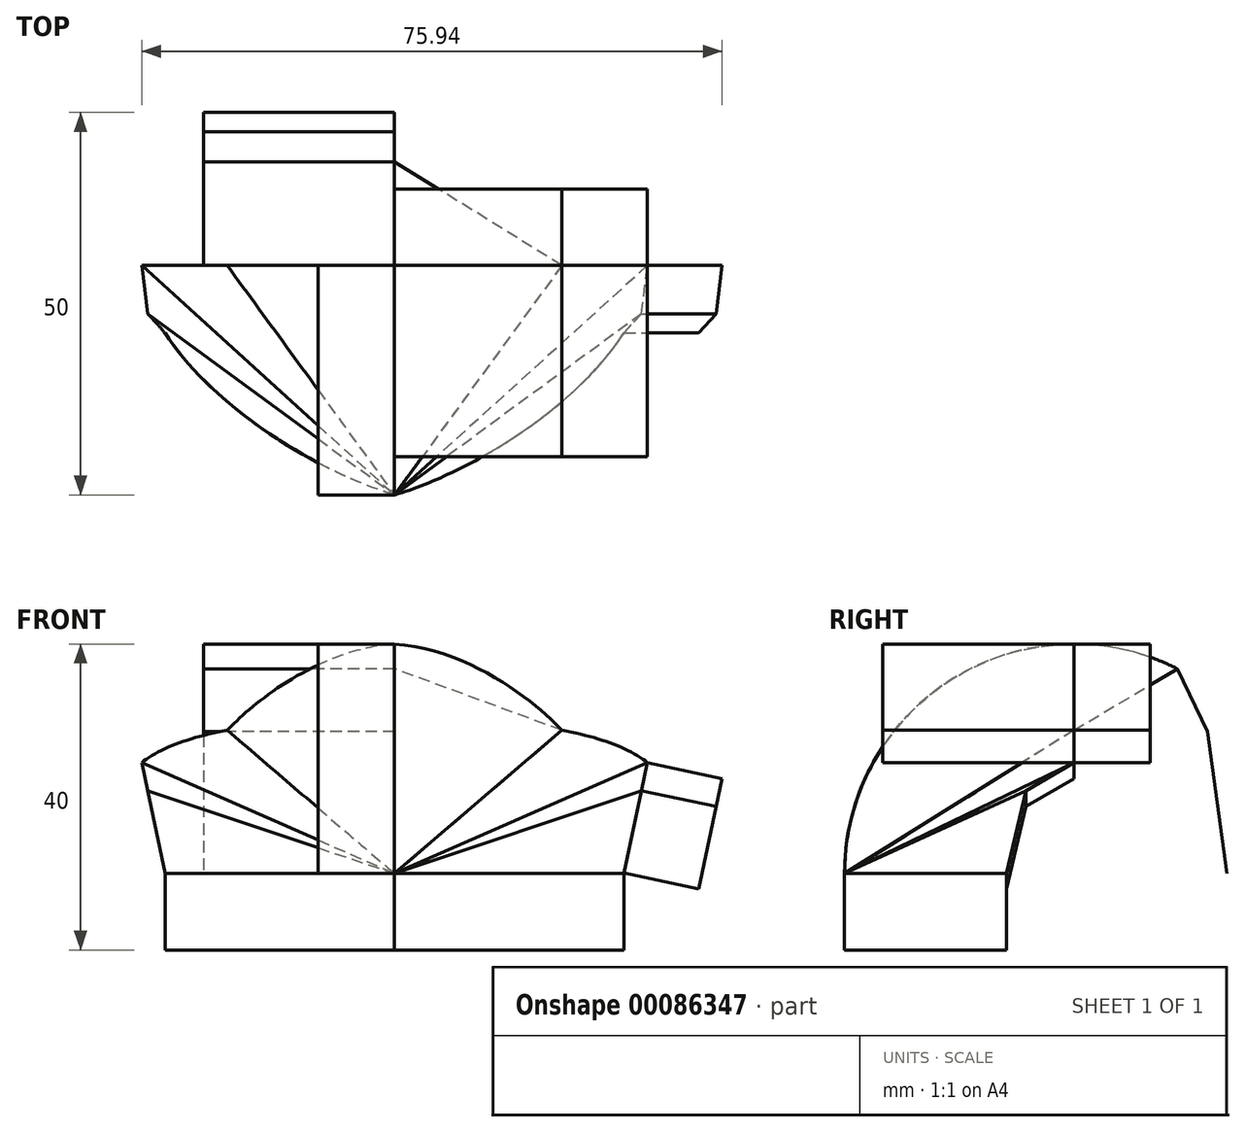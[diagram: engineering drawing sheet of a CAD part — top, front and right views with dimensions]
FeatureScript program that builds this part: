
annotation { "Feature Type Name" : "Feature", "Feature Type Description" : "" }
export const myFeature = defineFeature(function(context is Context, id is Id, definition is map)
    precondition{}
    {
        {
            var Q0;
            Q0=qCreatedBy(makeId("Front.planeOp"),FACE);
            var sketch = newSketch(context, id + "F0", { "sketchPlane" : qUnion([Q0])});
            skLineSegment(sketch, "E0", {"start": v(0, 0) * mm, "end": v(0, 30) * mm});
            skLineSegment(sketch, "E1", {"start": v(0, 0) * mm, "end": v(30, 0) * mm});
            skLineSegment(sketch, "E2", {"start": v(30, 0) * mm, "end": v(33.08, 14.5) * mm});
            skFitSpline(sketch, "E3", {"points": [v(0, 30) * mm, v(21.88, 18.74) * mm], "startDerivative": vector(30.88, -2.18) * mm, "endDerivative": vector(9.24, -9.83) * mm});
            skFitSpline(sketch, "E4", {"points": [v(33.08, 14.5) * mm, v(21.88, 18.74) * mm], "startDerivative": vector(-6.7, 5.6) * mm, "endDerivative": vector(-14.4, 2.61) * mm});
            skSolve(sketch);
        }
        {
            var Q0;
            Q0=qCreatedBy(makeId("Right.planeOp"),FACE);
            var sketch = newSketch(context, id + "F1", { "sketchPlane" : qUnion([Q0])});
            skLineSegment(sketch, "E5", {"start": v(-30, 0) * mm, "end": v(0, 0) * mm});
            skArc(sketch, "E6", {"start": v(0, 30) * mm, "mid": v(-21.21, 21.21) * mm, "end": v(-30, 0) * mm});
            skLineSegment(sketch, "E7", {"start": v(0, 30) * mm, "end": v(0, 0) * mm});
            skSolve(sketch);
        }
        {
            var Q0;
            Q0=qCreatedBy(makeId("Right.planeOp"),FACE);
            var Q1;
            Q1=sQuery(id+"F0.wireOp",EDGE,"E2");
            cPlane(context, id + "F2", {"entities" : qUnion([Q0, Q1]), "cplaneType" : CPlaneType.LINE_ANGLE, "offset" : 150 * mm, "angle" : 0 * degree, "width" : 150 * mm, "height" : 150 * mm});
        }
        {
            var Q0;
            Q0=qCreatedBy(id+"F2.planeOp",FACE);
            var sketch = newSketch(context, id + "F3", { "sketchPlane" : qUnion([Q0])});
            skLineSegment(sketch, "E8", {"start": v(6.3, 17.32) * mm, "end": v(0, 21.05) * mm});
            skLineSegment(sketch, "E9", {"start": v(0, 21.05) * mm, "end": v(0, 6.32) * mm});
            skLineSegment(sketch, "E10", {"start": v(6.3, 17.32) * mm, "end": v(8.79, 6.32) * mm});
            skLineSegment(sketch, "E11", {"start": v(0, 6.32) * mm, "end": v(8.79, 6.32) * mm});
            skSolve(sketch);
        }
        {
            var Q0;
            Q0=qCreatedBy(makeId("Top.planeOp"),FACE);
            var sketch = newSketch(context, id + "F4", { "sketchPlane" : qUnion([Q0])});
            skFitSpline(sketch, "E12", {"points": [v(0, -30) * mm, v(30, -8.8) * mm], "startDerivative": vector(34.32, 10.34) * mm, "endDerivative": vector(16.09, 25.94) * mm});
            skSolve(sketch);
        }
        {
            var Q0;
            Q0=sQuery(id+"F0.wireOp",EDGE,"E4");
            var Q1;
            Q1=sQuery(id+"F0.wireOp",EDGE,"E3");
            extrude(context, id + "F5", {"bodyType" : ToolBodyType.SURFACE, "surfaceEntities" : qUnion([Q0, Q1]), "oppositeDirection" : true, "depth" : 10 * mm});
        }
        {
            var Q0;
            Q0=sQuery(id+"F4.wireOp",EDGE,"E12");
            extrude(context, id + "F6", {"bodyType" : ToolBodyType.SURFACE, "surfaceEntities" : qUnion([Q0]), "oppositeDirection" : true, "depth" : 10 * mm});
        }
        {
            var Q0;
            Q0=sQuery(id+"F1.wireOp",EDGE,"E6");
            extrude(context, id + "F7", {"bodyType" : ToolBodyType.SURFACE, "surfaceEntities" : qUnion([Q0]), "oppositeDirection" : true, "depth" : 10 * mm});
        }
        {
            var Q0;
            Q0=sQuery(id+"F3.wireOp",EDGE,"E8");
            var Q1;
            Q1=sQuery(id+"F3.wireOp",EDGE,"E10");
            extrude(context, id + "F8", {"bodyType" : ToolBodyType.SURFACE, "surfaceEntities" : qUnion([Q0, Q1]), "oppositeDirection" : true, "depth" : 10 * mm});
        }
        {
            var Q0;
            Q0=makeQuery(id+"F5.opExtrude","SWEPT_BODY",BODY,{"disambiguationData":[OSD([sQuery(id+"F0.wireOp",EDGE,"E3")])]});
            var Q1;
            Q1=makeQuery(id+"F5.opExtrude","CAP_EDGE",EDGE,{"disambiguationData":[OSD([sQuery(id+"F0.wireOp",EDGE,"E3")])],"isStart":true});
            var Q2;
            Q2=makeQuery(id+"F7.opExtrude","CAP_EDGE",EDGE,{"disambiguationData":[OSD([sQuery(id+"F1.wireOp",EDGE,"E6")])],"isStart":true});
            loft(context, id + "F9", {"bodyType" : ToolBodyType.SURFACE, "sheetProfilesArray" : [{ "sheetProfileEntities" : qUnion([Q0]) }], "wireProfilesArray" : [{ "wireProfileEntities" : qUnion([Q1]) }, { "wireProfileEntities" : qUnion([Q2]) }]});
        }
        {
            var Q0;
            Q0=makeQuery(id+"F5.opExtrude","CAP_EDGE",EDGE,{"disambiguationData":[OSD([sQuery(id+"F0.wireOp",EDGE,"E4")])],"isStart":true});
            var Q1;
            Q1=makeQuery(id+"F9.opLoft","SWEPT_EDGE",EDGE,{"disambiguationData":[OSD([sQuery(id+"F0.wireOp",VERTEX,"E3.end"),sQuery(id+"F1.wireOp",VERTEX,"E6.end")])]});
            loft(context, id + "F10", {"bodyType" : ToolBodyType.SURFACE, "wireProfilesArray" : [{ "wireProfileEntities" : qUnion([Q0]) }, { "wireProfileEntities" : qUnion([Q1]) }]});
        }
        {
            var Q0;
            Q0=makeQuery(id+"F8.opExtrude","CAP_EDGE",EDGE,{"disambiguationData":[OSD([sQuery(id+"F3.wireOp",EDGE,"E8")])],"isStart":true});
            var Q1;
            Q1=makeQuery(id+"F10.opLoft","SWEPT_EDGE",EDGE,{"disambiguationData":[OSD([sQuery(id+"F0.wireOp",VERTEX,"E4.start"),sQuery(id+"F1.wireOp",VERTEX,"E6.end")])]});
            loft(context, id + "F11", {"bodyType" : ToolBodyType.SURFACE, "wireProfilesArray" : [{ "wireProfileEntities" : qUnion([Q0]) }, { "wireProfileEntities" : qUnion([Q1]) }]});
        }
        {
            var Q0;
            Q0=makeQuery(id+"F11.opLoft","SWEPT_EDGE",EDGE,{"disambiguationData":[OSD([sQuery(id+"F1.wireOp",VERTEX,"E6.end"),sQuery(id+"F3.wireOp",VERTEX,"E10.start")])]});
            var Q1;
            Q1=makeQuery(id+"F6.opExtrude","CAP_EDGE",EDGE,{"disambiguationData":[OSD([sQuery(id+"F4.wireOp",EDGE,"E12")])],"isStart":true});
            loft(context, id + "F12", {"bodyType" : ToolBodyType.SURFACE, "wireProfilesArray" : [{ "wireProfileEntities" : qUnion([Q0]) }, { "wireProfileEntities" : qUnion([Q1]) }]});
        }
        {
            var Q0;
            Q0=makeQuery(id+"F9.opLoft","SWEPT_BODY",BODY,{"disambiguationData":[OSD([sQuery(id+"F0.wireOp",EDGE,"E3"),sQuery(id+"F1.wireOp",EDGE,"E6")])]});
            var Q1;
            Q1=makeQuery(id+"F10.opLoft","SWEPT_BODY",BODY,{"disambiguationData":[OSD([sQuery(id+"F0.wireOp",VERTEX,"E3.end"),sQuery(id+"F0.wireOp",EDGE,"E4"),sQuery(id+"F1.wireOp",VERTEX,"E6.end")])]});
            var Q2;
            Q2=makeQuery(id+"F11.opLoft","SWEPT_BODY",BODY,{"disambiguationData":[OSD([sQuery(id+"F0.wireOp",VERTEX,"E4.start"),sQuery(id+"F1.wireOp",VERTEX,"E6.end"),sQuery(id+"F3.wireOp",EDGE,"E8")])]});
            var Q3;
            Q3=makeQuery(id+"F12.opLoft","SWEPT_BODY",BODY,{"disambiguationData":[OSD([sQuery(id+"F1.wireOp",VERTEX,"E6.end"),sQuery(id+"F3.wireOp",VERTEX,"E10.start"),sQuery(id+"F4.wireOp",EDGE,"E12")])]});
            var Q4;
            Q4=makeQuery(id+"F6.opExtrude","SWEPT_BODY",BODY,{"disambiguationData":[OSD([sQuery(id+"F4.wireOp",EDGE,"E12")])]});
            var Q5;
            Q5=qCreatedBy(makeId("Right.planeOp"),FACE);
            mirror(context, id + "F13", {"entities" : qUnion([Q0, Q1, Q2, Q3, Q4]), "mirrorPlane" : qUnion([Q5])});
        }
        {
            var Q0;
            Q0=qCreatedBy(makeId("Right.planeOp"),FACE);
            var sketch = newSketch(context, id + "F14", { "sketchPlane" : qUnion([Q0])});
            skCircle(sketch, "E13", {"center": v(0, 0) * mm, "radius": 30 * mm, "construction": true});
            skArc(sketch, "E14", {"start": v(13.56, 26.76) * mm, "mid": v(6.97, 29.18) * mm, "end": v(0, 30) * mm});
            skLineSegment(sketch, "E15", {"start": v(13.56, 26.76) * mm, "end": v(17.5, 18.55) * mm});
            skLineSegment(sketch, "E16", {"start": v(17.5, 18.55) * mm, "end": v(20, 0) * mm});
            skSolve(sketch);
        }
        {
            var Q0;
            Q0=qCreatedBy(makeId("Front.planeOp"),FACE);
            var Q1;
            Q1=sQuery(id+"F14.wireOp",EDGE,"E16");
            cPlane(context, id + "F15", {"entities" : qUnion([Q0, Q1]), "cplaneType" : CPlaneType.LINE_ANGLE, "offset" : 150 * mm, "angle" : 0 * degree, "width" : 150 * mm, "height" : 150 * mm});
        }
        {
            var Q0;
            Q0=sQuery(id+"F14.wireOp",EDGE,"E14");
            extrude(context, id + "F16", {"bodyType" : ToolBodyType.SURFACE, "surfaceEntities" : qUnion([Q0]), "oppositeDirection" : true, "depth" : 25 * mm});
        }
        {
            var Q0;
            Q0=sQuery(id+"F14.wireOp",EDGE,"E15");
            extrude(context, id + "F17", {"bodyType" : ToolBodyType.SURFACE, "surfaceEntities" : qUnion([Q0]), "oppositeDirection" : true, "depth" : 25 * mm});
        }
        {
            var Q0;
            Q0=sQuery(id+"F14.wireOp",EDGE,"E16");
            extrude(context, id + "F18", {"bodyType" : ToolBodyType.SURFACE, "surfaceEntities" : qUnion([Q0]), "oppositeDirection" : true, "depth" : 25 * mm});
        }
        {
            var Q0;
            Q0=sQuery(id+"F0.wireOp",EDGE,"E3");
            extrude(context, id + "F19", {"bodyType" : ToolBodyType.SURFACE, "surfaceEntities" : qUnion([Q0]), "depth" : 25 * mm});
        }
        {
            var Q0;
            Q0=sQuery(id+"F0.wireOp",EDGE,"E4");
            extrude(context, id + "F20", {"bodyType" : ToolBodyType.SURFACE, "surfaceEntities" : qUnion([Q0]), "depth" : 25 * mm});
        }
        {
            var Q0;
            Q0=sQuery(id+"F0.wireOp",EDGE,"E3");
            var Q1;
            Q1=sQuery(id+"F14.wireOp",EDGE,"E14");
            loft(context, id + "F21", {"bodyType" : ToolBodyType.SURFACE, "wireProfilesArray" : [{ "wireProfileEntities" : qUnion([Q0]) }, { "wireProfileEntities" : qUnion([Q1]) }]});
        }
    });
